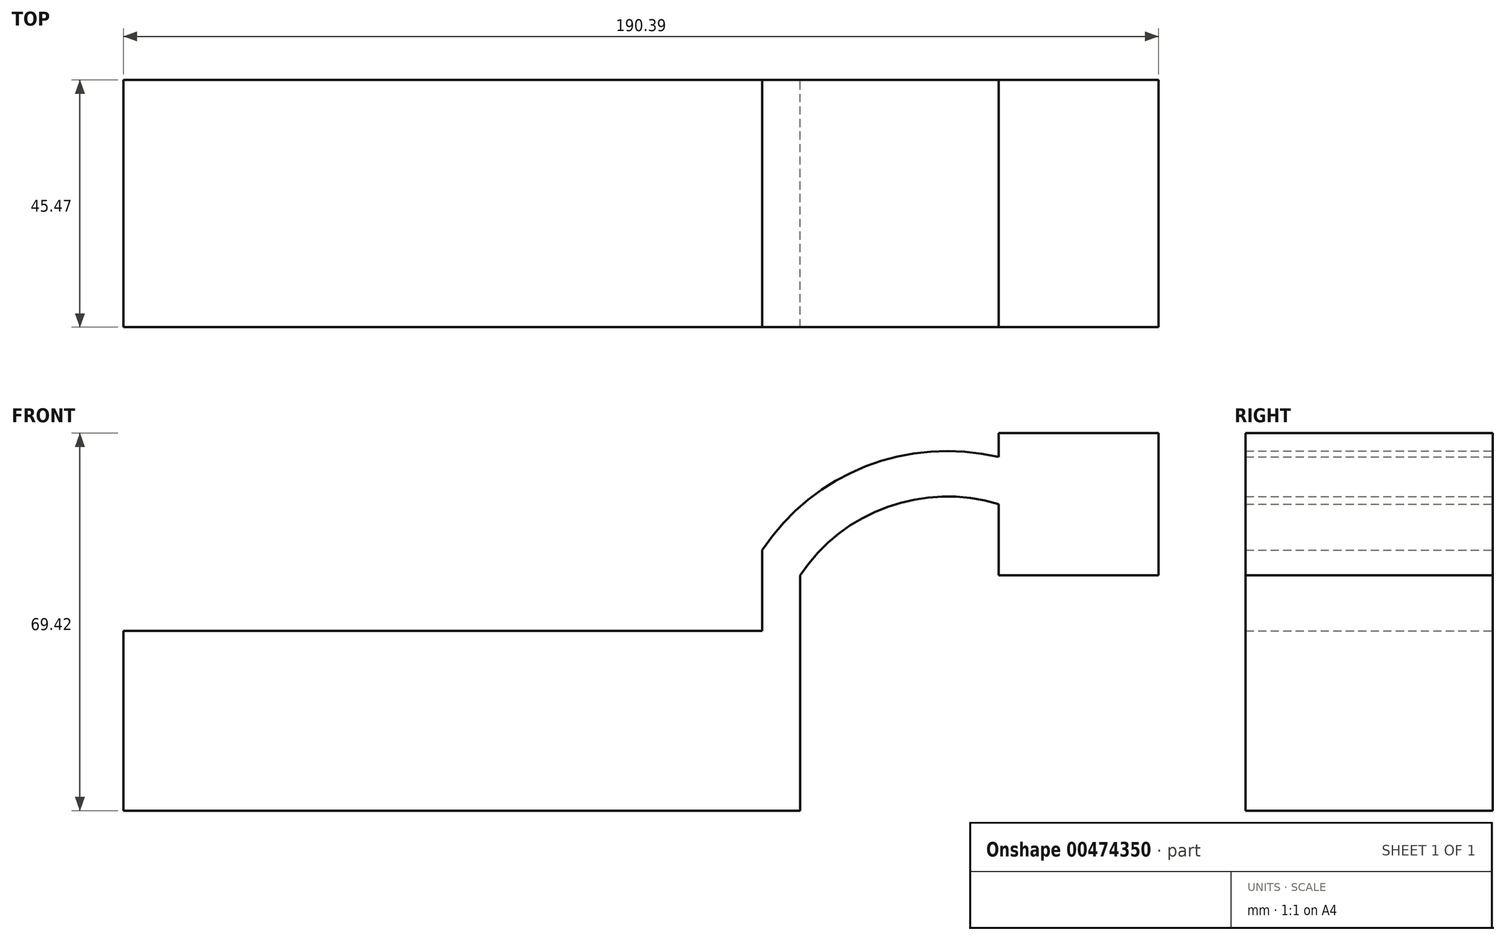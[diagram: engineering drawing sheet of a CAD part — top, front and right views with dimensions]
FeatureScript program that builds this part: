
annotation { "Feature Type Name" : "Feature", "Feature Type Description" : "" }
export const myFeature = defineFeature(function(context is Context, id is Id, definition is map)
    precondition{}
    {
        {
            var Q0;
            Q0=qCreatedBy(makeId("Front.planeOp"),FACE);
            var sketch = newSketch(context, id + "F0", { "sketchPlane" : qUnion([Q0])});
            skLineSegment(sketch, "E0.bottom", {"start": v(-61.54, 15.56) * mm, "end": v(62.92, 15.56) * mm});
            skLineSegment(sketch, "E0.top", {"start": v(-61.54, -17.5) * mm, "end": v(62.92, -17.5) * mm});
            skLineSegment(sketch, "E0.left", {"start": v(-61.54, 15.56) * mm, "end": v(-61.54, -17.5) * mm});
            skLineSegment(sketch, "E0.right", {"start": v(62.92, 15.56) * mm, "end": v(62.92, -17.5) * mm});
            skLineSegment(sketch, "E1.bottom", {"start": v(128.85, 51.92) * mm, "end": v(99.4, 51.92) * mm});
            skLineSegment(sketch, "E1.top", {"start": v(128.85, 25.8) * mm, "end": v(99.4, 25.8) * mm});
            skLineSegment(sketch, "E1.left", {"start": v(128.85, 51.92) * mm, "end": v(128.85, 25.8) * mm});
            skLineSegment(sketch, "E1.right", {"start": v(99.4, 51.92) * mm, "end": v(99.4, 25.8) * mm});
            skLineSegment(sketch, "E2", {"start": v(62.92, 15.56) * mm, "end": v(62.92, 25.8) * mm});
            skArc(sketch, "E3", {"start": v(99.4, 38.86) * mm, "mid": v(79, 38.37) * mm, "end": v(62.92, 25.8) * mm});
            skArc(sketch, "E4.0", {"start": v(99.4, 47.54) * mm, "mid": v(75, 45.82) * mm, "end": v(55.95, 30.45) * mm});
            skLineSegment(sketch, "E5", {"start": v(55.95, 30.45) * mm, "end": v(55.95, 15.56) * mm});
            skSolve(sketch);
        }
        {
            var Q0;
            {var subQ1=sQuery(id+"F0.wireOp",EDGE,"E2");Q0=makeQuery(id+"F0.imprint","IMPRINT",FACE,{"disambiguationData":[TD([[makeQuery(id+"F0.imprint","IMPRINT",EDGE,{"derivedFrom":subQ1}),1.0]])]});}
            var Q1;
            {var subQ1=sQuery(id+"F0.wireOp",EDGE,"E1.bottom");Q1=makeQuery(id+"F0.imprint","IMPRINT",FACE,{"disambiguationData":[TD([[makeQuery(id+"F0.imprint","IMPRINT",EDGE,{"derivedFrom":subQ1}),1.0]])]});}
            var Q2;
            Q2=makeQuery(id+"F0.imprint","IMPRINT",FACE,{"disambiguationData":[TD([[makeQuery(id+"F0.imprint","IMPRINT",EDGE,{"derivedFrom":sQuery(id+"F0.wireOp",EDGE,"E0.top")}),1.0]])]});
            extrude(context, id + "F1", {"entities" : qUnion([Q0, Q1, Q2]), "depth" : 45.47 * mm});
        }
    });
